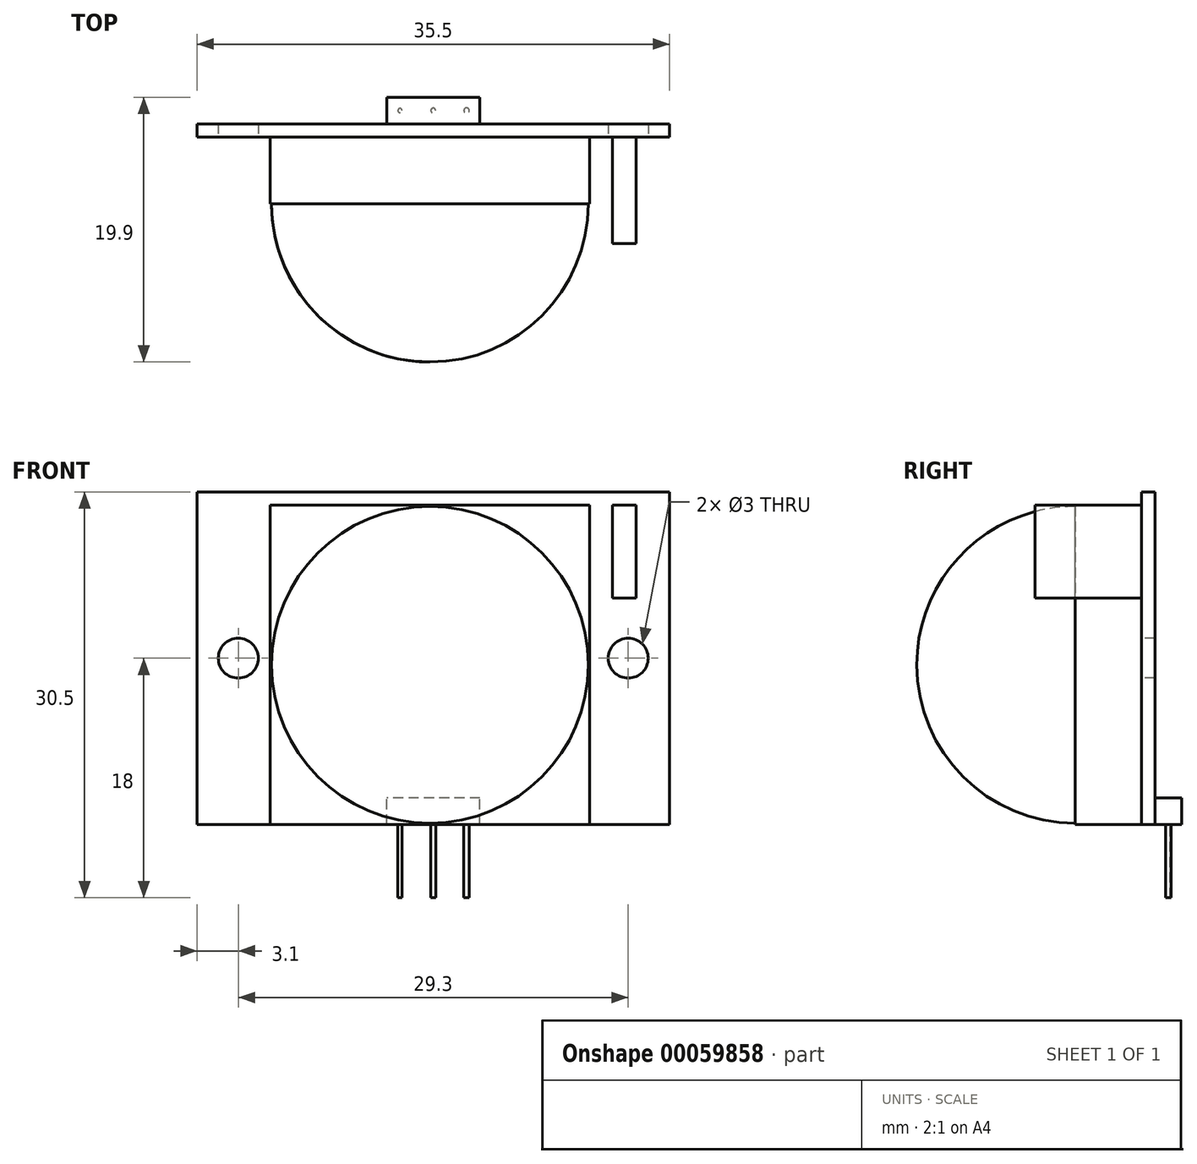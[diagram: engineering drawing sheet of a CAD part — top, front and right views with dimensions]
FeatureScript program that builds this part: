
annotation { "Feature Type Name" : "Feature", "Feature Type Description" : "" }
export const myFeature = defineFeature(function(context is Context, id is Id, definition is map)
    precondition{}
    {
        {
            var Q0;
            Q0=qCreatedBy(makeId("Front.planeOp"),FACE);
            var sketch = newSketch(context, id + "F0", { "sketchPlane" : qUnion([Q0])});
            skLineSegment(sketch, "E0.bottom", {"start": v(-17.75, 12.5) * mm, "end": v(17.75, 12.5) * mm});
            skLineSegment(sketch, "E0.top", {"start": v(-17.75, -12.5) * mm, "end": v(17.75, -12.5) * mm});
            skLineSegment(sketch, "E0.left", {"start": v(-17.75, 12.5) * mm, "end": v(-17.75, -12.5) * mm});
            skLineSegment(sketch, "E0.right", {"start": v(17.75, 12.5) * mm, "end": v(17.75, -12.5) * mm});
            skSolve(sketch);
        }
        {
            var Q0;
            Q0 = qSketchRegion(id + "F0", true);
            extrude(context, id + "F1", {"entities" : qUnion([Q0]), "oppositeDirection" : true, "depth" : 1 * mm});
        }
        {
            var Q0;
            Q0=makeQuery(id+"F1.opExtrude","CAP_FACE",FACE,{"disambiguationData":[OSD([sQuery(id+"F0.wireOp",EDGE,"E0.bottom"),sQuery(id+"F0.wireOp",EDGE,"E0.top"),sQuery(id+"F0.wireOp",EDGE,"E0.left"),sQuery(id+"F0.wireOp",EDGE,"E0.right")])],"isStart":true});
            var sketch = newSketch(context, id + "F2", { "sketchPlane" : qUnion([Q0])});
            skLineSegment(sketch, "E1.bottom", {"start": v(11.75, -12.5) * mm, "end": v(-12.25, -12.5) * mm});
            skLineSegment(sketch, "E1.top", {"start": v(11.75, 11.5) * mm, "end": v(-12.25, 11.5) * mm});
            skLineSegment(sketch, "E1.left", {"start": v(11.75, -12.5) * mm, "end": v(11.75, 11.5) * mm});
            skLineSegment(sketch, "E1.right", {"start": v(-12.25, -12.5) * mm, "end": v(-12.25, 11.5) * mm});
            skSolve(sketch);
        }
        {
            var Q0;
            Q0 = qSketchRegion(id + "F2", true);
            extrude(context, id + "F3", {"entities" : qUnion([Q0]), "operationType" : NewBodyOperationType.ADD, "depth" : 5 * mm});
        }
        {
            var Q0;
            Q0=qCreatedBy(makeId("Top.planeOp"),FACE);
            cPlane(context, id + "F4", {"entities" : qUnion([Q0]), "cplaneType" : CPlaneType.OFFSET, "offset" : 0.5 * mm, "oppositeDirection" : true, "width" : 150 * mm, "height" : 150 * mm});
        }
        {
            var Q0;
            Q0=qCreatedBy(id+"F4.planeOp",FACE);
            var sketch = newSketch(context, id + "F5", { "sketchPlane" : qUnion([Q0])});
            skLineSegment(sketch, "E2.0", {"start": v(11.75, -5) * mm, "end": v(-0.25, -5) * mm});
            skArc(sketch, "E3", {"start": v(-0.25, -16.9) * mm, "mid": v(8.16, -13.41) * mm, "end": v(11.65, -5) * mm});
            skLineSegment(sketch, "E4", {"start": v(-0.25, -5) * mm, "end": v(-0.25, -16.9) * mm});
            skLineSegment(sketch, "E5.trimOffspring", {"start": v(-12.15, -5) * mm, "end": v(-12.25, -5) * mm});
            skSolve(sketch);
        }
        {
            var Q0;
            Q0 = qSketchRegion(id + "F5", true);
            var Q1;
            Q1=sQuery(id+"F5.wireOp",EDGE,"E4");
            revolve(context, id + "F6", {"operationType" : NewBodyOperationType.ADD, "entities" : qUnion([Q0]), "axis" : qUnion([Q1]), "revolveType" : RevolveType.FULL});
        }
        {
            var Q0;
            Q0=makeQuery(id+"F1.opExtrude","CAP_FACE",FACE,{"disambiguationData":[OSD([sQuery(id+"F0.wireOp",EDGE,"E0.bottom"),sQuery(id+"F0.wireOp",EDGE,"E0.top"),sQuery(id+"F0.wireOp",EDGE,"E0.left"),sQuery(id+"F0.wireOp",EDGE,"E0.right")])],"isStart":true});
            var sketch = newSketch(context, id + "F7", { "sketchPlane" : qUnion([Q0])});
            skLineSegment(sketch, "E6.0", {"start": v(15.25, 4.5) * mm, "end": v(15.25, 11.5) * mm});
            skLineSegment(sketch, "E7.0", {"start": v(13.45, 4.5) * mm, "end": v(13.45, 11.5) * mm});
            skLineSegment(sketch, "E8", {"start": v(13.45, 11.5) * mm, "end": v(15.25, 11.5) * mm});
            skLineSegment(sketch, "E9", {"start": v(13.45, 4.5) * mm, "end": v(15.25, 4.5) * mm});
            skSolve(sketch);
        }
        {
            var Q0;
            Q0 = qSketchRegion(id + "F7", true);
            extrude(context, id + "F8", {"entities" : qUnion([Q0]), "operationType" : NewBodyOperationType.ADD, "depth" : 8 * mm});
        }
        {
            var Q0;
            Q0=makeQuery(id+"F1.opExtrude","CAP_FACE",FACE,{"disambiguationData":[OSD([sQuery(id+"F0.wireOp",EDGE,"E0.bottom"),sQuery(id+"F0.wireOp",EDGE,"E0.top"),sQuery(id+"F0.wireOp",EDGE,"E0.left"),sQuery(id+"F0.wireOp",EDGE,"E0.right")])],"isStart":true});
            var sketch = newSketch(context, id + "F9", { "sketchPlane" : qUnion([Q0])});
            skCircle(sketch, "E10", {"center": v(-14.65, 0) * mm, "radius": 1.5 * mm});
            skCircle(sketch, "E11", {"center": v(14.65, 0) * mm, "radius": 1.5 * mm});
            skSolve(sketch);
        }
        {
            var Q0;
            Q0 = qSketchRegion(id + "F9", true);
            extrude(context, id + "F10", {"entities" : qUnion([Q0]), "operationType" : NewBodyOperationType.REMOVE, "oppositeDirection" : true, "depth" : 25 * mm});
        }
        {
            var Q0;
            Q0=makeQuery(id+"F1.opExtrude","CAP_FACE",FACE,{"disambiguationData":[OSD([sQuery(id+"F0.wireOp",EDGE,"E0.bottom"),sQuery(id+"F0.wireOp",EDGE,"E0.top"),sQuery(id+"F0.wireOp",EDGE,"E0.left"),sQuery(id+"F0.wireOp",EDGE,"E0.right")])],"isStart":false});
            var sketch = newSketch(context, id + "F11", { "sketchPlane" : qUnion([Q0])});
            skLineSegment(sketch, "E12.bottom", {"start": v(-3.5, -12.5) * mm, "end": v(3.5, -12.5) * mm});
            skLineSegment(sketch, "E12.top", {"start": v(-3.5, -10.5) * mm, "end": v(3.5, -10.5) * mm});
            skLineSegment(sketch, "E12.left", {"start": v(-3.5, -12.5) * mm, "end": v(-3.5, -10.5) * mm});
            skLineSegment(sketch, "E12.right", {"start": v(3.5, -12.5) * mm, "end": v(3.5, -10.5) * mm});
            skSolve(sketch);
        }
        {
            var Q0;
            Q0 = qSketchRegion(id + "F11", true);
            extrude(context, id + "F12", {"entities" : qUnion([Q0]), "operationType" : NewBodyOperationType.ADD, "depth" : 2 * mm});
        }
        {
            var Q0;
            Q0=makeQuery(id+"F12.boolean.opBoolean","MERGE",FACE,{"derivedFrom":[makeQuery(id+"F3.boolean.opBoolean","MERGE",FACE,{"derivedFrom":[makeQuery(id+"F1.opExtrude","SWEPT_FACE",FACE,{"disambiguationData":[OSD([sQuery(id+"F0.wireOp",EDGE,"E0.top")])]}),makeQuery(id+"F3.opExtrude","SWEPT_FACE",FACE,{"disambiguationData":[OSD([sQuery(id+"F2.wireOp",EDGE,"E1.bottom")])]})]}),makeQuery(id+"F12.opExtrude","SWEPT_FACE",FACE,{"disambiguationData":[OSD([sQuery(id+"F11.wireOp",EDGE,"E12.bottom")])]})]});
            var sketch = newSketch(context, id + "F13", { "sketchPlane" : qUnion([Q0])});
            skCircle(sketch, "E13", {"center": v(2.5, -2) * mm, "radius": 0.2 * mm});
            skCircle(sketch, "E14", {"center": v(0, -2) * mm, "radius": 0.18 * mm});
            skCircle(sketch, "E15", {"center": v(-2.5, -2) * mm, "radius": 0.15 * mm});
            skSolve(sketch);
        }
        {
            var Q0;
            Q0 = qSketchRegion(id + "F13", true);
            extrude(context, id + "F14", {"entities" : qUnion([Q0]), "operationType" : NewBodyOperationType.ADD, "depth" : 5.5 * mm});
        }
    });
